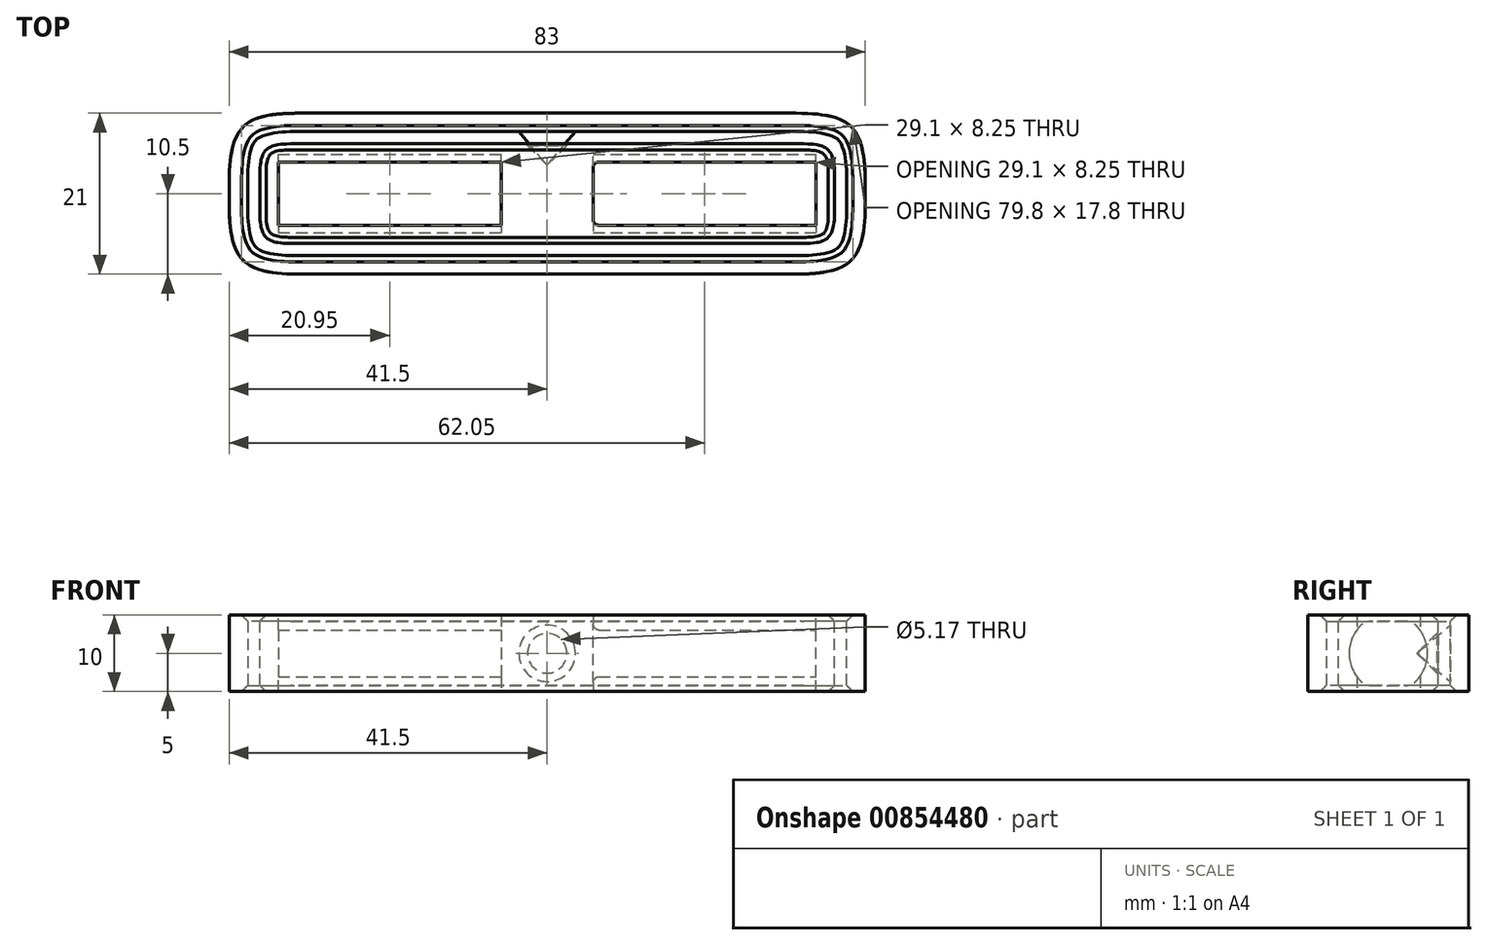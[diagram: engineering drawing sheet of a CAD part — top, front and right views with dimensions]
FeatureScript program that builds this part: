
annotation { "Feature Type Name" : "Feature", "Feature Type Description" : "" }
export const myFeature = defineFeature(function(context is Context, id is Id, definition is map)
    precondition{}
    {
        {
            assignVariable(context, id + "F0", {"name" : "depth", "anyValue" : 10});
        }
        {
            var Q0;
            Q0=qCreatedBy(makeId("Top.planeOp"),FACE);
            var sketch = newSketch(context, id + "F1", { "sketchPlane" : qUnion([Q0])});
            skLineSegment(sketch, "E0.bottom", {"start": v(41.5, 10.5) * mm, "end": v(-41.5, 10.5) * mm});
            skLineSegment(sketch, "E0.top", {"start": v(41.5, -10.5) * mm, "end": v(-41.5, -10.5) * mm});
            skLineSegment(sketch, "E0.left", {"start": v(41.5, 10.5) * mm, "end": v(41.5, -10.5) * mm});
            skLineSegment(sketch, "E0.right", {"start": v(-41.5, 10.5) * mm, "end": v(-41.5, -10.5) * mm});
            skPoint(sketch, "E0.middle", {"position": v(0, 0) * mm});
            skLineSegment(sketch, "E1.bottom", {"start": v(37.5, 6.5) * mm, "end": v(-37.5, 6.5) * mm});
            skLineSegment(sketch, "E1.top", {"start": v(37.5, -6.5) * mm, "end": v(-37.5, -6.5) * mm});
            skLineSegment(sketch, "E1.left", {"start": v(37.5, 6.5) * mm, "end": v(37.5, -6.5) * mm});
            skLineSegment(sketch, "E1.right", {"start": v(-37.5, 6.5) * mm, "end": v(-37.5, -6.5) * mm});
            skSolve(sketch);
        }
        {
            var Q0;
            Q0=makeQuery(id+"F1.imprint","IMPRINT",FACE,{"disambiguationData":[TD([[makeQuery(id+"F1.imprint","IMPRINT",EDGE,{"derivedFrom":sQuery(id+"F1.wireOp",EDGE,"E0.bottom")}),1.0]])]});
            var Q1;
            Q1=makeQuery(id+"F1.imprint","IMPRINT",FACE,{"disambiguationData":[TD([[makeQuery(id+"F1.imprint","IMPRINT",EDGE,{"derivedFrom":sQuery(id+"F1.wireOp",EDGE,"E1.bottom")}),1.0]])]});
            extrude(context, id + "F2", {"entities" : qUnion([Q0, Q1]), "endBound" : BoundingType.SYMMETRIC, "depth" : (getVariable(context, 'depth')) * mm, "offsetDistance" : 25 * mm});
        }
        {
            var Q0;
            Q0=makeQuery(id+"F2.opExtrude","SWEPT_EDGE",EDGE,{"disambiguationData":[OSD([sQuery(id+"F1.wireOp",EDGE,"E0.bottom"),sQuery(id+"F1.wireOp",EDGE,"E0.right")])]});
            var Q1;
            Q1=makeQuery(id+"F2.opExtrude","SWEPT_EDGE",EDGE,{"disambiguationData":[OSD([sQuery(id+"F1.wireOp",EDGE,"E0.top"),sQuery(id+"F1.wireOp",EDGE,"E0.right")])]});
            var Q2;
            Q2=makeQuery(id+"F2.opExtrude","SWEPT_EDGE",EDGE,{"disambiguationData":[OSD([sQuery(id+"F1.wireOp",EDGE,"E0.bottom"),sQuery(id+"F1.wireOp",EDGE,"E0.left")])]});
            var Q3;
            Q3=makeQuery(id+"F2.opExtrude","SWEPT_EDGE",EDGE,{"disambiguationData":[OSD([sQuery(id+"F1.wireOp",EDGE,"E0.top"),sQuery(id+"F1.wireOp",EDGE,"E0.left")])]});
            fillet(context, id + "F3", {"entities" : qUnion([Q0, Q1, Q2, Q3]), "radius" : 9 * mm, "tangentPropagation" : true, "rho" : .6, "crossSection" : FilletCrossSection.CONIC, "allowEdgeOverflow" : false});
        }
        {
            var Q0;
            Q0=makeQuery(id+"F2.opExtrude","CAP_FACE",FACE,{"disambiguationData":[OSD([sQuery(id+"F1.wireOp",EDGE,"E0.bottom"),sQuery(id+"F1.wireOp",EDGE,"E0.top"),sQuery(id+"F1.wireOp",EDGE,"E0.left"),sQuery(id+"F1.wireOp",EDGE,"E0.right")])],"isStart":false});
            var Q1;
            Q1=makeQuery(id+"F2.opExtrude","CAP_FACE",FACE,{"disambiguationData":[OSD([sQuery(id+"F1.wireOp",EDGE,"E0.bottom"),sQuery(id+"F1.wireOp",EDGE,"E0.top"),sQuery(id+"F1.wireOp",EDGE,"E0.left"),sQuery(id+"F1.wireOp",EDGE,"E0.right")])],"isStart":true});
            shell(context, id + "F4", {"entities" : qUnion([Q0, Q1]), "thickness" : 2.4 * mm});
        }
        {
            var Q0;
            Q0=makeQuery(id+"F1.imprint","IMPRINT",FACE,{"disambiguationData":[TD([[makeQuery(id+"F1.imprint","IMPRINT",EDGE,{"derivedFrom":sQuery(id+"F1.wireOp",EDGE,"E1.bottom")}),1.0]])]});
            extrude(context, id + "F5", {"entities" : qUnion([Q0]), "endBound" : BoundingType.SYMMETRIC, "depth" : (getVariable(context, 'depth')) * mm, "offsetDistance" : 25 * mm});
        }
        {
            var Q0;
            Q0=makeQuery(id+"F5.opExtrude","SWEPT_EDGE",EDGE,{"disambiguationData":[OSD([sQuery(id+"F1.wireOp",EDGE,"E1.bottom"),sQuery(id+"F1.wireOp",EDGE,"E1.right")])]});
            var Q1;
            Q1=makeQuery(id+"F5.opExtrude","SWEPT_EDGE",EDGE,{"disambiguationData":[OSD([sQuery(id+"F1.wireOp",EDGE,"E1.bottom"),sQuery(id+"F1.wireOp",EDGE,"E1.left")])]});
            var Q2;
            Q2=makeQuery(id+"F5.opExtrude","SWEPT_EDGE",EDGE,{"disambiguationData":[OSD([sQuery(id+"F1.wireOp",EDGE,"E1.top"),sQuery(id+"F1.wireOp",EDGE,"E1.left")])]});
            var Q3;
            Q3=makeQuery(id+"F5.opExtrude","SWEPT_EDGE",EDGE,{"disambiguationData":[OSD([sQuery(id+"F1.wireOp",EDGE,"E1.top"),sQuery(id+"F1.wireOp",EDGE,"E1.right")])]});
            fillet(context, id + "F6", {"entities" : qUnion([Q0, Q1, Q2, Q3]), "radius" : 4 * mm, "tangentPropagation" : true, "rho" : .6, "crossSection" : FilletCrossSection.CONIC, "allowEdgeOverflow" : false});
        }
        {
            var Q0;
            Q0=qCreatedBy(makeId("Right.planeOp"),FACE);
            var sketch = newSketch(context, id + "F7", { "sketchPlane" : qUnion([Q0])});
            skCircle(sketch, "E2", {"center": v(0, 0) * mm, "radius": 5.12 * mm});
            skLineSegment(sketch, "E3.bottom", {"start": v(4.12, 5) * mm, "end": v(-4.12, 5) * mm});
            skLineSegment(sketch, "E3.top", {"start": v(4.12, -5) * mm, "end": v(-4.12, -5) * mm});
            skLineSegment(sketch, "E3.left", {"start": v(4.12, 5) * mm, "end": v(4.12, -5) * mm});
            skLineSegment(sketch, "E3.right", {"start": v(-4.12, 5) * mm, "end": v(-4.12, -5) * mm});
            skLineSegment(sketch, "E4", {"start": v(4.12, 0) * mm, "end": v(5.12, 0) * mm, "construction": true});
            skSolve(sketch);
        }
        {
            var Q0;
            Q0 = qSketchRegion(id + "F7", true);
            var Q1;
            Q1=makeQuery(id+"F5.opExtrude","SWEPT_FACE",FACE,{"disambiguationData":[OSD([sQuery(id+"F1.wireOp",EDGE,"E1.right")])]});
            var Q2;
            Q2=makeQuery(id+"F5.opExtrude","SWEPT_FACE",FACE,{"disambiguationData":[OSD([sQuery(id+"F1.wireOp",EDGE,"E1.left")])]});
            extrude(context, id + "F8", {"entities" : qUnion([Q0]), "operationType" : NewBodyOperationType.REMOVE, "endBound" : BoundingType.UP_TO_SURFACE, "oppositeDirection" : true, "depth" : 70 * mm, "endBoundEntityFace" : qUnion([Q1]), "hasOffset" : true, "offsetDistance" : 2.4 * mm, "hasSecondDirection" : true, "secondDirectionBound" : SecondDirectionBoundingType.UP_TO_SURFACE, "secondDirectionOppositeDirection" : false, "secondDirectionDepth" : 25 * mm, "secondDirectionBoundEntityFace" : qUnion([Q2]), "hasSecondDirectionOffset" : true, "secondDirectionOffsetDistance" : 2.4 * mm});
        }
        {
            var Q0;
            {var subQ5=sQuery(id+"F7.wireOp",EDGE,"E3.top");Q0=makeQuery(id+"F7.imprint","IMPRINT",FACE,{"disambiguationData":[TD([[makeQuery(id+"F7.imprint","IMPRINT",EDGE,{"derivedFrom":subQ5}),-1.0]])]});}
            var Q1;
            {var subQ5=sQuery(id+"F7.wireOp",EDGE,"E3.bottom");Q1=makeQuery(id+"F7.imprint","IMPRINT",FACE,{"disambiguationData":[TD([[makeQuery(id+"F7.imprint","IMPRINT",EDGE,{"derivedFrom":subQ5}),1.0]])]});}
            var Q2;
            {var subQ0=sQuery(id+"F7.wireOp",EDGE,"E3.right");var subQ1=sQuery(id+"F7.wireOp",EDGE,"E2");var subQ2=makeQuery(id+"F7.imprint","INTERSECT",VERTEX,{"disambiguationData":[OD(0.0)],"derivedFrom":[subQ1,subQ0]});Q2=makeQuery(id+"F7.imprint","IMPRINT",FACE,{"disambiguationData":[TD([[makeQuery(id+"F7.imprint","IMPRINT",EDGE,{"disambiguationData":[TD([[subQ2,1.0]])],"derivedFrom":subQ1}),1.0]])]});}
            var Q3;
            {var subQ0=sQuery(id+"F7.wireOp",EDGE,"E3.left");var subQ1=sQuery(id+"F7.wireOp",EDGE,"E2");var subQ2=makeQuery(id+"F7.imprint","INTERSECT",VERTEX,{"disambiguationData":[OD(0.0)],"derivedFrom":[subQ1,subQ0]});Q3=makeQuery(id+"F7.imprint","IMPRINT",FACE,{"disambiguationData":[TD([[makeQuery(id+"F7.imprint","IMPRINT",EDGE,{"disambiguationData":[TD([[subQ2,1.0]])],"derivedFrom":subQ1}),1.0]])]});}
            var Q4;
            {var subQ0=sQuery(id+"F7.wireOp",EDGE,"E3.right");var subQ1=sQuery(id+"F7.wireOp",EDGE,"E2");var subQ2=makeQuery(id+"F7.imprint","INTERSECT",VERTEX,{"disambiguationData":[OD(0.0)],"derivedFrom":[subQ1,subQ0]});Q4=makeQuery(id+"F7.imprint","IMPRINT",FACE,{"disambiguationData":[TD([[makeQuery(id+"F7.imprint","IMPRINT",EDGE,{"disambiguationData":[TD([[subQ2,-1.0]])],"derivedFrom":subQ1}),1.0]])]});}
            extrude(context, id + "F9", {"entities" : qUnion([Q0, Q1, Q2, Q3, Q4]), "operationType" : NewBodyOperationType.ADD, "endBound" : BoundingType.SYMMETRIC, "depth" : 12 * mm, "offsetDistance" : 25 * mm});
        }
        {
            var Q0;
            Q0=qCreatedBy(makeId("Right.planeOp"),FACE);
            var sketch = newSketch(context, id + "F10", { "sketchPlane" : qUnion([Q0])});
            skLineSegment(sketch, "E5", {"start": v(8.1, 3.7) * mm, "end": v(3.7, 0) * mm, "construction": true});
            skLineSegment(sketch, "E6", {"start": v(3.7, 0) * mm, "end": v(8.1, -3.7) * mm, "construction": true});
            skLineSegment(sketch, "E7", {"start": v(8.1, 3.7) * mm, "end": v(8.1, -3.7) * mm, "construction": true});
            skArc(sketch, "E8", {"start": v(4.07, 0.3) * mm, "mid": v(3.92, 0) * mm, "end": v(4.07, -0.3) * mm, "construction": true});
            skLineSegment(sketch, "E9", {"start": v(0, 0) * mm, "end": v(3.7, 0) * mm, "construction": true});
            skLineSegment(sketch, "E10", {"start": v(4.32, 0) * mm, "end": v(3.7, 0) * mm, "construction": true});
            skLineSegment(sketch, "E11", {"start": v(6.5, 2.78) * mm, "end": v(3.72, 0) * mm, "construction": true});
            skLineSegment(sketch, "E12", {"start": v(3.72, 0) * mm, "end": v(6.5, -2.78) * mm, "construction": true});
            skLineSegment(sketch, "E13", {"start": v(6.5, -2.78) * mm, "end": v(6.5, 2.78) * mm, "construction": true});
            skLineSegment(sketch, "E14", {"start": v(6.5, 2.58) * mm, "end": v(6.3, 2.58) * mm, "construction": true});
            skLineSegment(sketch, "E15", {"start": v(6.5, -2.58) * mm, "end": v(6.3, -2.58) * mm, "construction": true});
            skLineSegment(sketch, "E16", {"start": v(3.72, 0) * mm, "end": v(8.1, 0) * mm, "construction": true});
            skSolve(sketch);
        }
        {
            var Q0;
            Q0=qCreatedBy(makeId("Right.planeOp"),FACE);
            var sketch = newSketch(context, id + "F11", { "sketchPlane" : qUnion([Q0])});
            skLineSegment(sketch, "E17", {"start": v(8.1, 0) * mm, "end": v(3.92, 0) * mm});
            skLineSegment(sketch, "E18", {"start": v(4.07, -0.3) * mm, "end": v(8.1, -3.7) * mm});
            skLineSegment(sketch, "E19", {"start": v(8.1, -3.7) * mm, "end": v(8.1, 0) * mm});
            skArc(sketch, "E20", {"start": v(3.92, 0) * mm, "mid": v(3.96, -0.17) * mm, "end": v(4.07, -0.3) * mm});
            skPoint(sketch, "E21.orphan", {"position": v(3.7, 0) * mm});
            skSolve(sketch);
        }
        {
            var Q0;
            Q0=qCreatedBy(makeId("Right.planeOp"),FACE);
            var sketch = newSketch(context, id + "F12", { "sketchPlane" : qUnion([Q0])});
            skLineSegment(sketch, "E22", {"start": v(6.5, 0) * mm, "end": v(3.72, 0) * mm});
            skLineSegment(sketch, "E23", {"start": v(3.72, 0) * mm, "end": v(6.3, -2.58) * mm});
            skLineSegment(sketch, "E24", {"start": v(6.3, -2.58) * mm, "end": v(6.5, -2.58) * mm});
            skLineSegment(sketch, "E25", {"start": v(6.5, -2.58) * mm, "end": v(6.5, 0) * mm});
            skSolve(sketch);
        }
        {
            var Q0;
            Q0 = qSketchRegion(id + "F12", true);
            var Q1;
            Q1=sQuery(id+"F10.wireOp",EDGE,"E9");
            revolve(context, id + "F13", {"operationType" : NewBodyOperationType.REMOVE, "surfaceOperationType" : NewSurfaceOperationType.NEW, "entities" : qUnion([Q0]), "axis" : qUnion([Q1]), "revolveType" : RevolveType.FULL, "oppositeDirection" : true});
        }
        {
            var Q0;
            Q0 = qSketchRegion(id + "F11", true);
            var Q1;
            Q1=sQuery(id+"F11.wireOp",EDGE,"E17");
            revolve(context, id + "F14", {"operationType" : NewBodyOperationType.ADD, "surfaceOperationType" : NewSurfaceOperationType.NEW, "entities" : qUnion([Q0]), "axis" : qUnion([Q1]), "revolveType" : RevolveType.FULL});
        }
        {
            var Q0;
            {var subQ0=sQuery(id+"F7.wireOp",EDGE,"E3.left");Q0=makeQuery(id+"F8.boolean.opBoolean","COPY",EDGE,{"derivedFrom":makeQuery(id+"F8.opExtrude","TWEAK_EDGE",EDGE,{"derivedFrom":[makeQuery(id+"F5.opExtrude","SWEPT_FACE",FACE,{"disambiguationData":[OSD([sQuery(id+"F1.wireOp",EDGE,"E1.left")])]}),makeQuery(id+"F7.imprint","IMPRINT",EDGE,{"disambiguationData":[TD([[makeQuery(id+"F7.imprint","INTERSECT",VERTEX,{"derivedFrom":[sQuery(id+"F7.wireOp",EDGE,"E3.top"),subQ0]}),1.0]])],"derivedFrom":subQ0})]})});}
            var Q1;
            {var subQ0=sQuery(id+"F7.wireOp",EDGE,"E3.left");Q1=makeQuery(id+"F8.boolean.opBoolean","COPY",EDGE,{"derivedFrom":makeQuery(id+"F8.opExtrude","TWEAK_EDGE",EDGE,{"derivedFrom":[makeQuery(id+"F5.opExtrude","SWEPT_FACE",FACE,{"disambiguationData":[OSD([sQuery(id+"F1.wireOp",EDGE,"E1.left")])]}),makeQuery(id+"F7.imprint","IMPRINT",EDGE,{"disambiguationData":[TD([[makeQuery(id+"F7.imprint","INTERSECT",VERTEX,{"derivedFrom":[sQuery(id+"F7.wireOp",EDGE,"E3.bottom"),subQ0]}),-1.0]])],"derivedFrom":subQ0})]})});}
            var Q2;
            {var subQ0=sQuery(id+"F7.wireOp",EDGE,"E3.right");Q2=makeQuery(id+"F8.boolean.opBoolean","COPY",EDGE,{"derivedFrom":makeQuery(id+"F8.opExtrude","TWEAK_EDGE",EDGE,{"derivedFrom":[makeQuery(id+"F5.opExtrude","SWEPT_FACE",FACE,{"disambiguationData":[OSD([sQuery(id+"F1.wireOp",EDGE,"E1.left")])]}),makeQuery(id+"F7.imprint","IMPRINT",EDGE,{"disambiguationData":[TD([[makeQuery(id+"F7.imprint","INTERSECT",VERTEX,{"derivedFrom":[sQuery(id+"F7.wireOp",EDGE,"E3.bottom"),subQ0]}),-1.0]])],"derivedFrom":subQ0})]})});}
            var Q3;
            {var subQ0=sQuery(id+"F7.wireOp",EDGE,"E3.right");Q3=makeQuery(id+"F8.boolean.opBoolean","COPY",EDGE,{"derivedFrom":makeQuery(id+"F8.opExtrude","TWEAK_EDGE",EDGE,{"derivedFrom":[makeQuery(id+"F5.opExtrude","SWEPT_FACE",FACE,{"disambiguationData":[OSD([sQuery(id+"F1.wireOp",EDGE,"E1.left")])]}),makeQuery(id+"F7.imprint","IMPRINT",EDGE,{"disambiguationData":[TD([[makeQuery(id+"F7.imprint","INTERSECT",VERTEX,{"derivedFrom":[sQuery(id+"F7.wireOp",EDGE,"E3.top"),subQ0]}),1.0]])],"derivedFrom":subQ0})]})});}
            var Q4;
            {var subQ0=sQuery(id+"F7.wireOp",EDGE,"E3.left");Q4=makeQuery(id+"F9.opExtrude","CAP_EDGE",EDGE,{"disambiguationData":[OSD([subQ0]),TDD([makeQuery(id+"F7.imprint","IMPRINT",EDGE,{"disambiguationData":[TD([[makeQuery(id+"F7.imprint","INTERSECT",VERTEX,{"derivedFrom":[sQuery(id+"F7.wireOp",EDGE,"E3.top"),subQ0]}),1.0]])],"derivedFrom":subQ0})])],"isStart":false});}
            var Q5;
            {var subQ0=sQuery(id+"F7.wireOp",EDGE,"E3.left");Q5=makeQuery(id+"F9.opExtrude","CAP_EDGE",EDGE,{"disambiguationData":[OSD([subQ0]),TDD([makeQuery(id+"F7.imprint","IMPRINT",EDGE,{"disambiguationData":[TD([[makeQuery(id+"F7.imprint","INTERSECT",VERTEX,{"derivedFrom":[sQuery(id+"F7.wireOp",EDGE,"E3.bottom"),subQ0]}),-1.0]])],"derivedFrom":subQ0})])],"isStart":false});}
            var Q6;
            {var subQ0=sQuery(id+"F7.wireOp",EDGE,"E3.right");Q6=makeQuery(id+"F9.opExtrude","CAP_EDGE",EDGE,{"disambiguationData":[OSD([subQ0]),TDD([makeQuery(id+"F7.imprint","IMPRINT",EDGE,{"disambiguationData":[TD([[makeQuery(id+"F7.imprint","INTERSECT",VERTEX,{"derivedFrom":[sQuery(id+"F7.wireOp",EDGE,"E3.bottom"),subQ0]}),-1.0]])],"derivedFrom":subQ0})])],"isStart":false});}
            var Q7;
            {var subQ0=sQuery(id+"F7.wireOp",EDGE,"E3.right");Q7=makeQuery(id+"F9.opExtrude","CAP_EDGE",EDGE,{"disambiguationData":[OSD([subQ0]),TDD([makeQuery(id+"F7.imprint","IMPRINT",EDGE,{"disambiguationData":[TD([[makeQuery(id+"F7.imprint","INTERSECT",VERTEX,{"derivedFrom":[sQuery(id+"F7.wireOp",EDGE,"E3.top"),subQ0]}),1.0]])],"derivedFrom":subQ0})])],"isStart":false});}
            var Q8;
            {var subQ0=sQuery(id+"F7.wireOp",EDGE,"E3.right");Q8=makeQuery(id+"F9.opExtrude","CAP_EDGE",EDGE,{"disambiguationData":[OSD([subQ0]),TDD([makeQuery(id+"F7.imprint","IMPRINT",EDGE,{"disambiguationData":[TD([[makeQuery(id+"F7.imprint","INTERSECT",VERTEX,{"derivedFrom":[sQuery(id+"F7.wireOp",EDGE,"E3.top"),subQ0]}),1.0]])],"derivedFrom":subQ0})])],"isStart":true});}
            var Q9;
            {var subQ0=sQuery(id+"F7.wireOp",EDGE,"E3.right");Q9=makeQuery(id+"F9.opExtrude","CAP_EDGE",EDGE,{"disambiguationData":[OSD([subQ0]),TDD([makeQuery(id+"F7.imprint","IMPRINT",EDGE,{"disambiguationData":[TD([[makeQuery(id+"F7.imprint","INTERSECT",VERTEX,{"derivedFrom":[sQuery(id+"F7.wireOp",EDGE,"E3.bottom"),subQ0]}),-1.0]])],"derivedFrom":subQ0})])],"isStart":true});}
            var Q10;
            {var subQ0=sQuery(id+"F7.wireOp",EDGE,"E3.left");Q10=makeQuery(id+"F9.opExtrude","CAP_EDGE",EDGE,{"disambiguationData":[OSD([subQ0]),TDD([makeQuery(id+"F7.imprint","IMPRINT",EDGE,{"disambiguationData":[TD([[makeQuery(id+"F7.imprint","INTERSECT",VERTEX,{"derivedFrom":[sQuery(id+"F7.wireOp",EDGE,"E3.top"),subQ0]}),1.0]])],"derivedFrom":subQ0})])],"isStart":true});}
            var Q11;
            {var subQ0=sQuery(id+"F7.wireOp",EDGE,"E3.left");Q11=makeQuery(id+"F9.opExtrude","CAP_EDGE",EDGE,{"disambiguationData":[OSD([subQ0]),TDD([makeQuery(id+"F7.imprint","IMPRINT",EDGE,{"disambiguationData":[TD([[makeQuery(id+"F7.imprint","INTERSECT",VERTEX,{"derivedFrom":[sQuery(id+"F7.wireOp",EDGE,"E3.bottom"),subQ0]}),-1.0]])],"derivedFrom":subQ0})])],"isStart":true});}
            var Q12;
            {var subQ0=sQuery(id+"F7.wireOp",EDGE,"E3.left");Q12=makeQuery(id+"F8.boolean.opBoolean","COPY",EDGE,{"derivedFrom":makeQuery(id+"F8.opExtrude","TWEAK_EDGE",EDGE,{"derivedFrom":[makeQuery(id+"F5.opExtrude","SWEPT_FACE",FACE,{"disambiguationData":[OSD([sQuery(id+"F1.wireOp",EDGE,"E1.right")])]}),makeQuery(id+"F7.imprint","IMPRINT",EDGE,{"disambiguationData":[TD([[makeQuery(id+"F7.imprint","INTERSECT",VERTEX,{"derivedFrom":[sQuery(id+"F7.wireOp",EDGE,"E3.top"),subQ0]}),1.0]])],"derivedFrom":subQ0})]})});}
            var Q13;
            {var subQ0=sQuery(id+"F7.wireOp",EDGE,"E3.left");Q13=makeQuery(id+"F8.boolean.opBoolean","COPY",EDGE,{"derivedFrom":makeQuery(id+"F8.opExtrude","TWEAK_EDGE",EDGE,{"derivedFrom":[makeQuery(id+"F5.opExtrude","SWEPT_FACE",FACE,{"disambiguationData":[OSD([sQuery(id+"F1.wireOp",EDGE,"E1.right")])]}),makeQuery(id+"F7.imprint","IMPRINT",EDGE,{"disambiguationData":[TD([[makeQuery(id+"F7.imprint","INTERSECT",VERTEX,{"derivedFrom":[sQuery(id+"F7.wireOp",EDGE,"E3.bottom"),subQ0]}),-1.0]])],"derivedFrom":subQ0})]})});}
            var Q14;
            {var subQ0=sQuery(id+"F7.wireOp",EDGE,"E3.right");Q14=makeQuery(id+"F8.boolean.opBoolean","COPY",EDGE,{"derivedFrom":makeQuery(id+"F8.opExtrude","TWEAK_EDGE",EDGE,{"derivedFrom":[makeQuery(id+"F5.opExtrude","SWEPT_FACE",FACE,{"disambiguationData":[OSD([sQuery(id+"F1.wireOp",EDGE,"E1.right")])]}),makeQuery(id+"F7.imprint","IMPRINT",EDGE,{"disambiguationData":[TD([[makeQuery(id+"F7.imprint","INTERSECT",VERTEX,{"derivedFrom":[sQuery(id+"F7.wireOp",EDGE,"E3.top"),subQ0]}),1.0]])],"derivedFrom":subQ0})]})});}
            var Q15;
            {var subQ0=sQuery(id+"F7.wireOp",EDGE,"E3.right");Q15=makeQuery(id+"F8.boolean.opBoolean","COPY",EDGE,{"derivedFrom":makeQuery(id+"F8.opExtrude","TWEAK_EDGE",EDGE,{"derivedFrom":[makeQuery(id+"F5.opExtrude","SWEPT_FACE",FACE,{"disambiguationData":[OSD([sQuery(id+"F1.wireOp",EDGE,"E1.right")])]}),makeQuery(id+"F7.imprint","IMPRINT",EDGE,{"disambiguationData":[TD([[makeQuery(id+"F7.imprint","INTERSECT",VERTEX,{"derivedFrom":[sQuery(id+"F7.wireOp",EDGE,"E3.bottom"),subQ0]}),-1.0]])],"derivedFrom":subQ0})]})});}
            fillet(context, id + "F15", {"entities" : qUnion([Q0, Q1, Q2, Q3, Q4, Q5, Q6, Q7, Q8, Q9, Q10, Q11, Q12, Q13, Q14, Q15]), "radius" : .75 * mm, "tangentPropagation" : true, "allowEdgeOverflow" : false});
        }
        {
            var Q0;
            {var subQ0=sQuery(id+"F1.wireOp",EDGE,"E0.bottom");Q0=makeQuery(id+"F4.opShell","OFFSET_EDGE",EDGE,{"disambiguationData":[OSD([subQ0]),TDD([makeQuery(id+"F2.opExtrude","CAP_EDGE",EDGE,{"disambiguationData":[OSD([subQ0])],"isStart":false})])]});}
            var Q1;
            {var subQ0=sQuery(id+"F1.wireOp",EDGE,"E0.right");Q1=makeQuery(id+"F4.opShell","OFFSET_EDGE",EDGE,{"disambiguationData":[OSD([subQ0]),TDD([makeQuery(id+"F2.opExtrude","CAP_EDGE",EDGE,{"disambiguationData":[OSD([subQ0])],"isStart":true})])]});}
            var Q2;
            Q2=makeQuery(id+"F5.opExtrude","CAP_EDGE",EDGE,{"disambiguationData":[OSD([sQuery(id+"F1.wireOp",EDGE,"E1.right")])],"isStart":true});
            var Q3;
            Q3=makeQuery(id+"F5.opExtrude","CAP_EDGE",EDGE,{"disambiguationData":[OSD([sQuery(id+"F1.wireOp",EDGE,"E1.right")])],"isStart":false});
            chamfer(context, id + "F16", {"entities" : qUnion([Q0, Q1, Q2, Q3]), "width" : .8 * mm, "tangentPropagation" : true});
        }
    });
